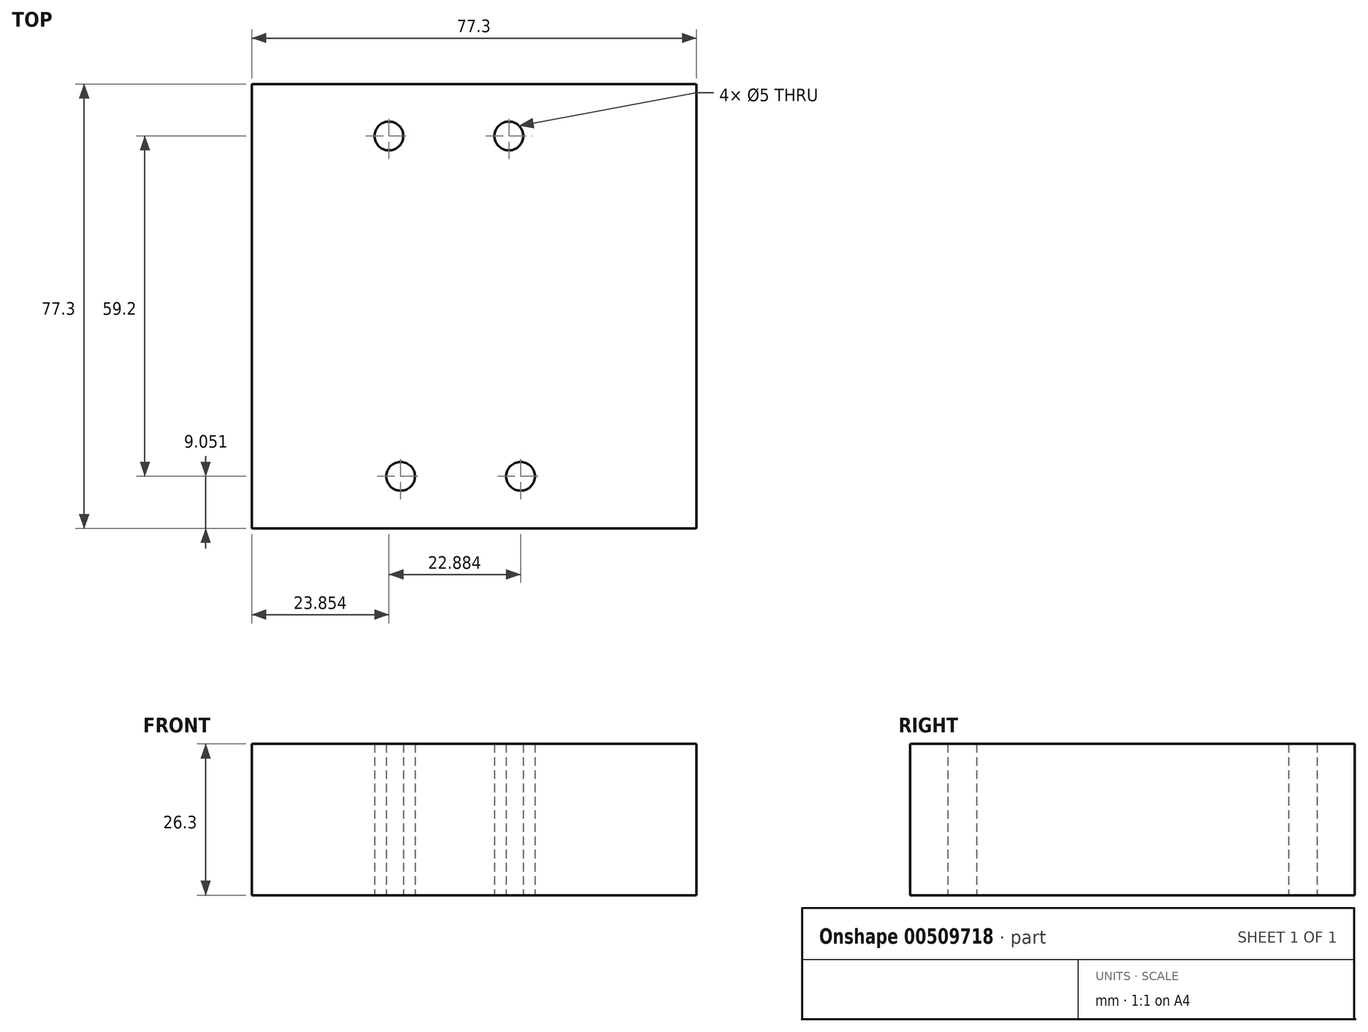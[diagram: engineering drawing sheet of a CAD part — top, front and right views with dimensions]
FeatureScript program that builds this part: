
annotation { "Feature Type Name" : "Feature", "Feature Type Description" : "" }
export const myFeature = defineFeature(function(context is Context, id is Id, definition is map)
    precondition{}
    {
        {
            var Q0;
            Q0=qCreatedBy(makeId("Top.planeOp"),FACE);
            var sketch = newSketch(context, id + "F0", { "sketchPlane" : qUnion([Q0])});
            skLineSegment(sketch, "E0.bottom", {"start": v(38.65, -18.9) * mm, "end": v(-38.65, -18.9) * mm});
            skLineSegment(sketch, "E0.top", {"start": v(38.65, 58.4) * mm, "end": v(-38.65, 58.4) * mm});
            skLineSegment(sketch, "E0.left", {"start": v(38.65, -18.9) * mm, "end": v(38.65, 58.4) * mm});
            skLineSegment(sketch, "E0.right", {"start": v(-38.65, -18.9) * mm, "end": v(-38.65, 58.4) * mm});
            skPoint(sketch, "E0.middle", {"position": v(0, 19.75) * mm});
            skSolve(sketch);
        }
        {
            var Q0;
            Q0 = qSketchRegion(id + "F0", true);
            extrude(context, id + "F1", {"entities" : qUnion([Q0]), "depth" : 26.3 * mm});
        }
        {
            var Q0;
            Q0=qCreatedBy(makeId("Top.planeOp"),FACE);
            var sketch = newSketch(context, id + "F2", { "sketchPlane" : qUnion([Q0])});
            skCircle(sketch, "E1", {"center": v(-12.76, -9.85) * mm, "radius": 2.5 * mm});
            skCircle(sketch, "E2", {"center": v(8.09, -9.85) * mm, "radius": 2.5 * mm});
            skCircle(sketch, "E3", {"center": v(6.05, 49.35) * mm, "radius": 2.5 * mm});
            skCircle(sketch, "E4", {"center": v(-14.8, 49.35) * mm, "radius": 2.5 * mm});
            skSolve(sketch);
        }
        {
            var Q0;
            Q0 = qSketchRegion(id + "F2", true);
            extrude(context, id + "F3", {"entities" : qUnion([Q0]), "operationType" : NewBodyOperationType.REMOVE, "depth" : 66.5 * mm});
        }
    });
